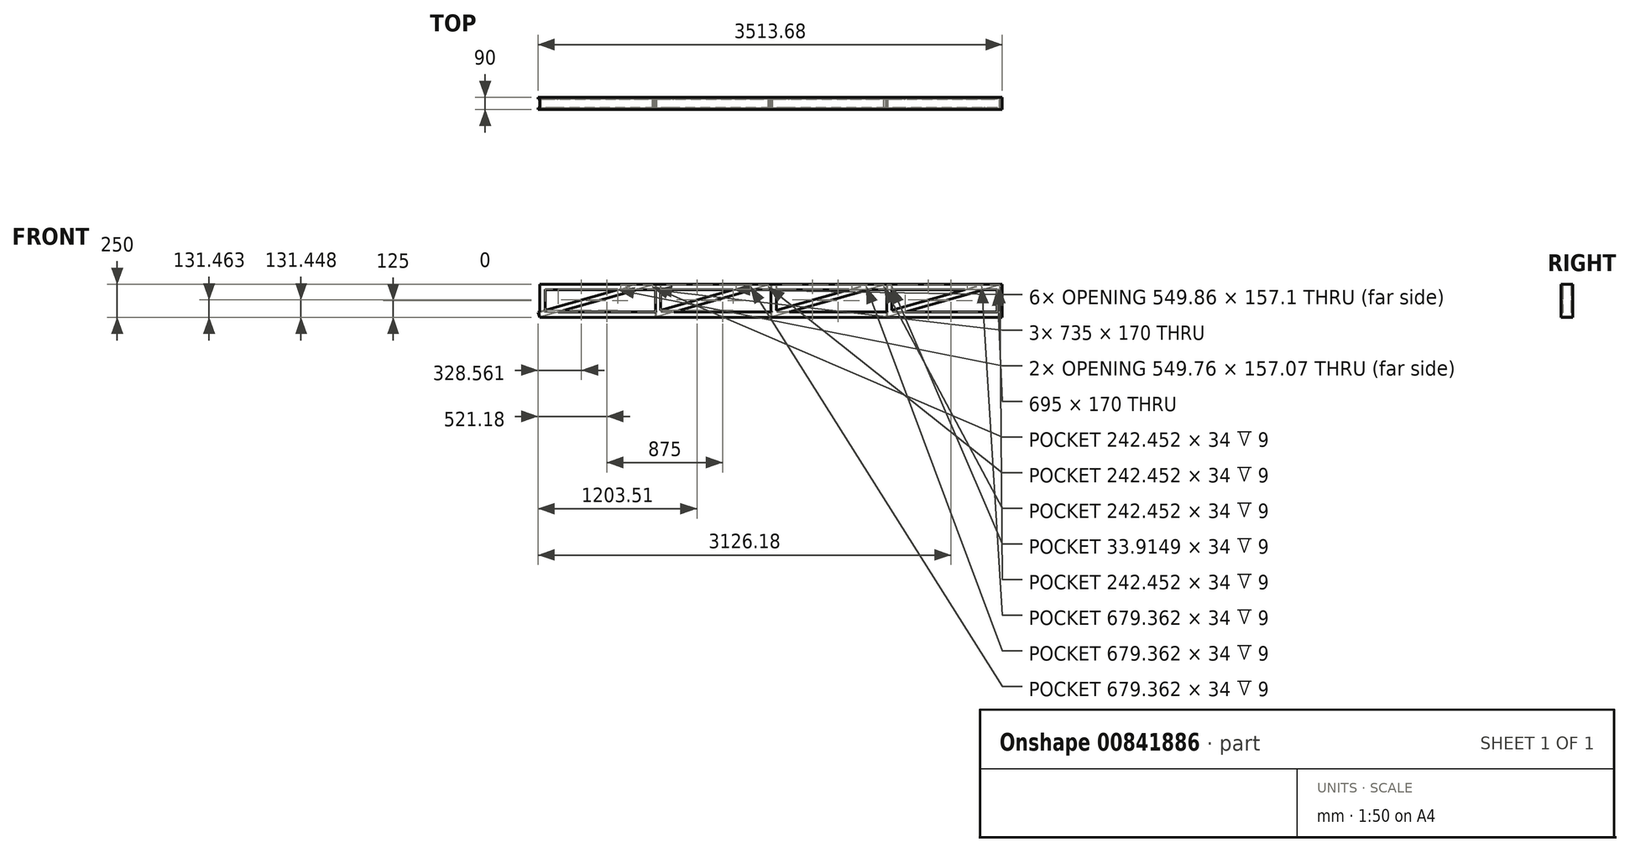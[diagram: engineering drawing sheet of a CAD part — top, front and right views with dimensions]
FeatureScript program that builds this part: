
annotation { "Feature Type Name" : "Feature", "Feature Type Description" : "" }
export const myFeature = defineFeature(function(context is Context, id is Id, definition is map)
    precondition{}
    {
        {
            var Q0;
            Q0=qCreatedBy(makeId("Front.planeOp"),FACE);
            var sketch = newSketch(context, id + "F0", { "sketchPlane" : qUnion([Q0])});
            skLineSegment(sketch, "E0.bottom", {"start": v(0, 0) * mm, "end": v(3500, 0) * mm});
            skLineSegment(sketch, "E0.top", {"start": v(0, 250) * mm, "end": v(3500, 250) * mm});
            skLineSegment(sketch, "E0.left", {"start": v(0, 0) * mm, "end": v(0, 250) * mm});
            skLineSegment(sketch, "E0.right", {"start": v(3500, 0) * mm, "end": v(3500, 250) * mm});
            skSolve(sketch);
        }
        {
            var Q0;
            Q0=qCreatedBy(makeId("Top.planeOp"),FACE);
            var sketch = newSketch(context, id + "F1", { "sketchPlane" : qUnion([Q0])});
            skLineSegment(sketch, "E1", {"start": v(0, 0) * mm, "end": v(0, -45) * mm});
            skLineSegment(sketch, "E2", {"start": v(0, -45) * mm, "end": v(40, -45) * mm});
            skLineSegment(sketch, "E3", {"start": v(40, -45) * mm, "end": v(40, -33) * mm});
            skLineSegment(sketch, "E4.MirrorCS", {"start": v(0, 0) * mm, "end": v(0, 45) * mm});
            skLineSegment(sketch, "E5.MirrorCS", {"start": v(0, 45) * mm, "end": v(40, 45) * mm});
            skLineSegment(sketch, "E6.MirrorCS", {"start": v(40, 45) * mm, "end": v(40, 33) * mm});
            skLineSegment(sketch, "E7.0", {"start": v(37, -42) * mm, "end": v(37, -33) * mm});
            skLineSegment(sketch, "E7.1", {"start": v(3, -42) * mm, "end": v(37, -42) * mm});
            skLineSegment(sketch, "E7.2", {"start": v(37, 42) * mm, "end": v(37, 33) * mm});
            skLineSegment(sketch, "E7.3", {"start": v(3, 42) * mm, "end": v(37, 42) * mm});
            skLineSegment(sketch, "E7.4", {"start": v(3, 0) * mm, "end": v(3, 42) * mm});
            skLineSegment(sketch, "E7.5", {"start": v(3, 0) * mm, "end": v(3, -42) * mm});
            skLineSegment(sketch, "E8", {"start": v(37, -33) * mm, "end": v(40, -33) * mm});
            skLineSegment(sketch, "E9", {"start": v(40, 33) * mm, "end": v(37, 33) * mm});
            skSolve(sketch);
        }
        {
            var Q0;
            Q0=makeQuery(id+"F1.imprint","IMPRINT",FACE,{"disambiguationData":[TD([[makeQuery(id+"F1.imprint","IMPRINT",EDGE,{"derivedFrom":sQuery(id+"F1.wireOp",EDGE,"E1")}),1.0]])]});
            var Q1;
            Q1=sQuery(id+"F0.wireOp",EDGE,"E0.top");
            var Q2;
            Q2=sQuery(id+"F0.wireOp",EDGE,"E0.left");
            var Q3;
            Q3=sQuery(id+"F0.wireOp",EDGE,"E0.right");
            var Q4;
            Q4=sQuery(id+"F0.wireOp",EDGE,"E0.bottom");
            sweep(context, id + "F2", {"profiles" : qUnion([Q0]), "path" : qUnion([Q1, Q2, Q3, Q4])});
        }
        {
            var Q0;
            Q0=qCreatedBy(makeId("Front.planeOp"),FACE);
            var sketch = newSketch(context, id + "F3", { "sketchPlane" : qUnion([Q0])});
            skLineSegment(sketch, "E10", {"start": v(0, 0) * mm, "end": v(875, 250) * mm});
            skLineSegment(sketch, "E11", {"start": v(875, 250) * mm, "end": v(875, 0) * mm});
            skLineSegment(sketch, "E12", {"start": v(875, 0) * mm, "end": v(1750, 250) * mm});
            skLineSegment(sketch, "E13", {"start": v(1750, 250) * mm, "end": v(1750, 0) * mm});
            skLineSegment(sketch, "E14", {"start": v(1750, 0) * mm, "end": v(2625, 250) * mm});
            skLineSegment(sketch, "E15", {"start": v(2625, 250) * mm, "end": v(2625, 0) * mm});
            skLineSegment(sketch, "E16", {"start": v(2625, 0) * mm, "end": v(3500, 250) * mm});
            skSolve(sketch);
        }
        {
            var Q0;
            Q0=makeQuery(id+"F2.opSweep","CAP_EDGE",EDGE,{"disambiguationData":[OSD([sQuery(id+"F0.wireOp",VERTEX,"E0.bottom.start"),sQuery(id+"F1.wireOp",EDGE,"E1"),sQuery(id+"F1.wireOp",EDGE,"E4.MirrorCS")])],"isStart":true});
            cPlane(context, id + "F4", {"entities" : qUnion([Q0]), "cplaneType" : CPlaneType.LINE_ANGLE, "offset" : 25 * mm, "angle" : 70 * degree, "width" : 150 * mm, "height" : 150 * mm});
        }
        {
            var Q0;
            Q0=qCreatedBy(id+"F4.planeOp",FACE);
            var sketch = newSketch(context, id + "F5", { "sketchPlane" : qUnion([Q0])});
            skLineSegment(sketch, "E17", {"start": v(0, 0) * mm, "end": v(45, 0) * mm});
            skLineSegment(sketch, "E18", {"start": v(45, 0) * mm, "end": v(45, 40) * mm});
            skLineSegment(sketch, "E19", {"start": v(45, 40) * mm, "end": v(33, 40) * mm});
            skLineSegment(sketch, "E20.MirrorCS", {"start": v(-45, 40) * mm, "end": v(-33, 40) * mm});
            skLineSegment(sketch, "E21.MirrorCS", {"start": v(-45, 0) * mm, "end": v(-45, 40) * mm});
            skLineSegment(sketch, "E22.MirrorCS", {"start": v(0, 0) * mm, "end": v(-45, 0) * mm});
            skLineSegment(sketch, "E23.0", {"start": v(42, 37) * mm, "end": v(33, 37) * mm});
            skLineSegment(sketch, "E23.1", {"start": v(42, 3) * mm, "end": v(42, 37) * mm});
            skLineSegment(sketch, "E23.2", {"start": v(-42, 37) * mm, "end": v(-33, 37) * mm});
            skLineSegment(sketch, "E23.3", {"start": v(-42, 3) * mm, "end": v(-42, 37) * mm});
            skLineSegment(sketch, "E23.4", {"start": v(0, 3) * mm, "end": v(-42, 3) * mm});
            skLineSegment(sketch, "E23.5", {"start": v(0, 3) * mm, "end": v(42, 3) * mm});
            skLineSegment(sketch, "E24.0", {"start": v(-40, 5) * mm, "end": v(-40, 229.92) * mm});
            skLineSegment(sketch, "E24.1", {"start": v(40, 5) * mm, "end": v(-40, 5) * mm});
            skLineSegment(sketch, "E24.2", {"start": v(40, 229.92) * mm, "end": v(40, 5) * mm});
            skLineSegment(sketch, "E24.3", {"start": v(40, 229.92) * mm, "end": v(-40, 229.92) * mm});
            skLineSegment(sketch, "E25", {"start": v(33, 40) * mm, "end": v(33, 37) * mm});
            skLineSegment(sketch, "E26", {"start": v(-33, 40) * mm, "end": v(-33, 37) * mm});
            skSolve(sketch);
        }
        {
            var Q0;
            Q0=makeQuery(id+"F5.imprint","IMPRINT",FACE,{"disambiguationData":[TD([[makeQuery(id+"F5.imprint","IMPRINT",EDGE,{"derivedFrom":sQuery(id+"F5.wireOp",EDGE,"E17")}),1.0]])]});
            var Q1;
            {var subQ0=sQuery(id+"F5.wireOp",EDGE,"E26");Q1=makeQuery(id+"F5.imprint","IMPRINT",FACE,{"disambiguationData":[TD([[makeQuery(id+"F5.imprint","IMPRINT",EDGE,{"derivedFrom":subQ0}),-1.0]])]});}
            var Q2;
            {var subQ0=sQuery(id+"F5.wireOp",EDGE,"E25");Q2=makeQuery(id+"F5.imprint","IMPRINT",FACE,{"disambiguationData":[TD([[makeQuery(id+"F5.imprint","IMPRINT",EDGE,{"derivedFrom":subQ0}),1.0]])]});}
            var Q3;
            Q3=sQuery(id+"F3.wireOp",EDGE,"E10");
            var Q4;
            Q4=sQuery(id+"F3.wireOp",EDGE,"E11");
            var Q5;
            Q5=sQuery(id+"F3.wireOp",EDGE,"E12");
            var Q6;
            Q6=sQuery(id+"F3.wireOp",EDGE,"E13");
            var Q7;
            Q7=sQuery(id+"F3.wireOp",EDGE,"E14");
            var Q8;
            Q8=sQuery(id+"F3.wireOp",EDGE,"E15");
            var Q9;
            Q9=sQuery(id+"F3.wireOp",EDGE,"E16");
            sweep(context, id + "F6", {"operationType" : NewBodyOperationType.ADD, "profiles" : qUnion([Q0, Q1, Q2]), "path" : qUnion([Q3, Q4, Q5, Q6, Q7, Q8, Q9])});
        }
        {
            var Q0;
            Q0=makeQuery(id+"F2.opSweep","SWEPT_FACE",FACE,{"disambiguationData":[OSD([sQuery(id+"F0.wireOp",EDGE,"E0.right"),sQuery(id+"F1.wireOp",EDGE,"E1"),sQuery(id+"F1.wireOp",EDGE,"E4.MirrorCS")])]});
            var sketch = newSketch(context, id + "F7", { "sketchPlane" : qUnion([Q0])});
            skLineSegment(sketch, "E27.bottom", {"start": v(-45, 250) * mm, "end": v(48.14, 250) * mm});
            skLineSegment(sketch, "E27.top", {"start": v(-45, 306.78) * mm, "end": v(48.14, 306.78) * mm});
            skLineSegment(sketch, "E27.left", {"start": v(-45, 250) * mm, "end": v(-45, 306.78) * mm});
            skLineSegment(sketch, "E27.right", {"start": v(48.14, 250) * mm, "end": v(48.14, 306.78) * mm});
            skSolve(sketch);
        }
        {
            var Q0;
            Q0 = qSketchRegion(id + "F7", true);
            extrude(context, id + "F8", {"entities" : qUnion([Q0]), "operationType" : NewBodyOperationType.REMOVE, "endBound" : BoundingType.THROUGH_ALL, "oppositeDirection" : true, "depth" : 25 * mm, "offsetDistance" : 25 * mm});
        }
    });
